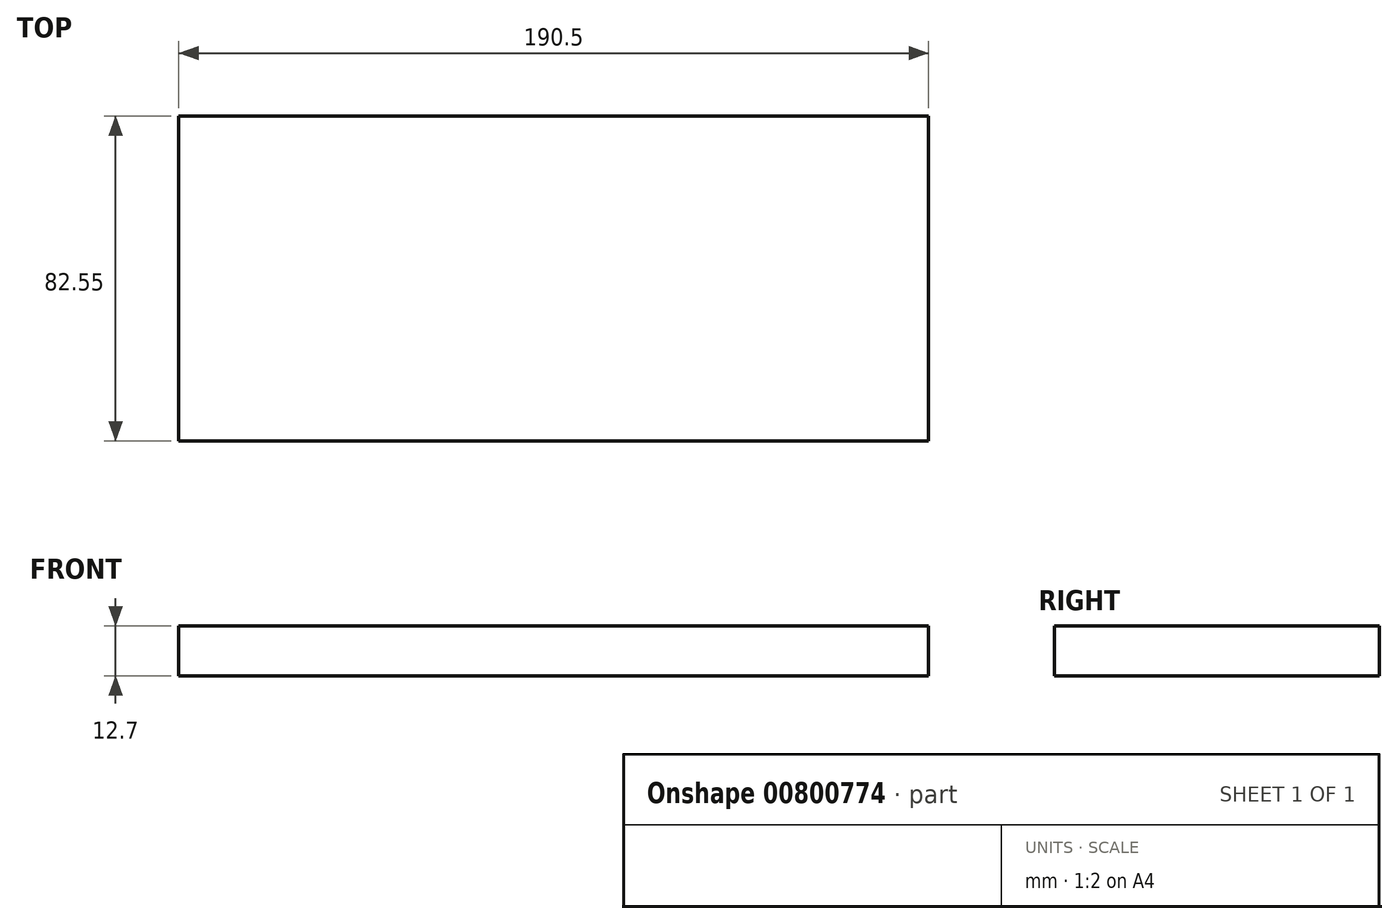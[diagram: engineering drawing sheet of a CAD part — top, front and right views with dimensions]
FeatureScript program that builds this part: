
annotation { "Feature Type Name" : "Feature", "Feature Type Description" : "" }
export const myFeature = defineFeature(function(context is Context, id is Id, definition is map)
    precondition{}
    {
        {
            var Q0;
            Q0=qCreatedBy(makeId("Front.planeOp"),FACE);
            var sketch = newSketch(context, id + "F0", { "sketchPlane" : qUnion([Q0])});
            skLineSegment(sketch, "E0", {"start": v(0, 0) * mm, "end": v(190.5, 0) * mm});
            skLineSegment(sketch, "E1", {"start": v(190.5, 0) * mm, "end": v(190.5, 12.7) * mm});
            skLineSegment(sketch, "E2", {"start": v(190.5, 12.7) * mm, "end": v(0, 12.7) * mm});
            skLineSegment(sketch, "E3", {"start": v(0, 12.7) * mm, "end": v(0, 0) * mm});
            skSolve(sketch);
        }
        {
            var Q0;
            Q0=makeQuery(id+"F0.imprint","IMPRINT",FACE,{"disambiguationData":[TD([[makeQuery(id+"F0.imprint","IMPRINT",EDGE,{"derivedFrom":sQuery(id+"F0.wireOp",EDGE,"E0")}),1.0]])]});
            extrude(context, id + "F1", {"entities" : qUnion([Q0]), "depth" : 82.55 * mm, "offsetDistance" : 25.4 * mm});
        }
    });
